# Revit family: GALAD Арктур LED проба2
name_source: partatom
category: Осветительные приборы
revit_build: Autodesk Revit 2018 (Build: 20180423_1000(x64)
units: mm (PartAtom-declared; Revit-internal decimal feet)

## family parameters
Источник света = Да
Общий = Нет
Основа = Грань
При загрузке вырезать с полостями = Нет
Размер круглого соединителя = Использовать диаметр
Тип детали = Нормальный
Точка расчета площади = Нет

## types (1)
- Семейство2
    ADSK_Версия Revit = 2018
    ADSK_Версия семейства = 1.01
    ADSK_Единица измерения = шт.
    ADSK_Завод-изготовитель = АО «КАДОШКИНСКИЙ ЭЛЕКТРОТЕХНИЧЕСКИЙ ЗАВОД»
    ADSK_Классификация нагрузок = Освещение
    ADSK_Код изделия = 4299
    ADSK_Количество = 1
    ADSK_Количество фаз = 1
    ADSK_Коэффициент мощности = 0.98
    ADSK_Марка = ДДУ21-1-001 Арктур
    ADSK_Масса = 0.29
    ADSK_Масса_Текст = 0.29
    ADSK_Наименование = ДДУ21-1-001 Арктур
    ADSK_Наименование краткое = ДДУ21-1-001 Арктур
    ADSK_Напряжение = 36 В
    ADSK_Номинальная мощность = 1 В·А
    ADSK_Обозначение = ГОСТ
    ADSK_Полная мощность = 1 В·А
    ADSK_Размер_Высота = 31 мм
    ADSK_Размер_Длина = 90 мм
    ADSK_Размер_Ширина = 90 мм
    ADSK_Ток = 0 А
    IP = 67
    URL = https://galad.ru
    Возможный угол наклона = 0
    Группа модели = ДДУ21
    Изготовитель = АО «КАДОШКИНСКИЙ ЭЛЕКТРОТЕХНИЧЕСКИЙ ЗАВОД»
    Класс Защиты = 1
    Класс защиты от поражения электрическим током = 3
    Класс светораспределения = П
    Климатическая зона = У2
    Климатическое исполнение = -45…40 °С
    Коэффициент пульсации = менее 5%
    Материал корпуса = Нержавеющая сталь
    Материал рассеивателя = ПММА
    Неравномерность яркости = 0
    Область использования = Тонельный
    Описание = Светильник GALAD Арктур LED предназначен для обозначения края дорожного полотна и горизонтального габарита тоннеля и выдерживает нагрузку до 5 тонн. Устанавливается на дорожное полотно в крайней правой полосе движения транспорта как можно ближе к бордюру или стеновой панели тоннеля, или на бордюр. Внутри корпуса в двух противоположных сторонах находятся две светодиодные линейки (с белыми и красными светодиодами).
    Отметка по умолчанию = 1219 мм
    Размер обозначения источников света = 610 мм
    Световая отдача = 0
    Светофильтр = 16777215
    Смещение цветовой температуры при затухании лампы = <Нет>
    Снижение светового потока во время разгорания = не более 6%
    Срок службы = 12 лет
    Тип ПРА = ЭПРА
    Тип источника света = LED
    Тип монтажной поверхности = стена/пол/потолок
    Тип продукции = Светильник
    Тип устройства управления светодиодами = без управления
    Цветопередача = 0
    Частота = 50
